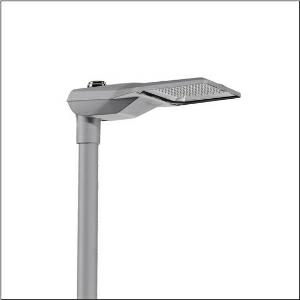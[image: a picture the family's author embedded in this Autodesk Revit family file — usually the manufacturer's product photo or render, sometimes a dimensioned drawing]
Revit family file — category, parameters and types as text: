
# Revit family: streetlight_sl_21_midi___p1_0a_5xe7a47n08mb_40bb
name_source: partatom
category: Lighting Fixtures
units: mm (PartAtom-declared; Revit-internal decimal feet)

## family parameters
Cut with Voids When Loaded = No
Host = Face
Light Source = No
Part Type = Normal
Room Calculation Point = No
Round Connector Dimension = Use Diameter
Shared = No

## types (1)
- --- (1 x LED, 20180 lm, 147 W, 4000K)
    Apparent Load = 147 VA
    CIE Flux Codes = 21 50 90 100 100
    Color Rendering = 70
    Color Temperature = 4000K
    Default Elevation = 1800 mm
    Description = Streetlight SL 21 midi, mast luminaire, primary light control with lens, of PMMA, primary optical cover: cover, of toughened safety glass, transparent, light distribution: P1.0a, light emission: direct distribution, primary light characteristic: asymmetric, installation type: side-entry, LED, 3G 2.5mm², High Power LED, rated luminous flux: 20.180lm, luminous efficacy: 137lm/W, light colour: 740, colour temperature: 4000K, control gear: NEMA (7pin), control: overheat protection, pre-setting: linear dimming characteristic, constant luminous flux control, time-dependent luminous flux control, flexible luminous flux parameterisation, mains connection: 220..240V, AC, 50/60Hz, connection cable pre-assembled, cable length: 12,5m, wiring characteristics: H05VV-F, start of lifetime: 147W, end of service life: 155W, reduction: 65W, luminaire housing, of diecast aluminium (EN AC-44300), powder-coated, Siteco® metallic grey (DB 702S), corrosivity category C5 mid according to DIN EN ISO 12944, multi-level sealing system, sealing non-destructively replaceable, inclination adjustable: 0°, 5°, 10°, 15°, length: 644mm, width: 335mm, height: 110mm, spigot size: 42mm (side-entry), mounting height: 4..8m, protection rating (complete): IP66, insulation class (complete): insulation class I (protective earthing), certification: CE, ENEC, ENEC+, VDE, impact resistance: IK10, permissible operating ambient temperature for outdoor applications: -40..+50°C, standard-compliant lighting for roads and squares, packaging unit: 1 piece

Light Distribution: P1.0a
    Height = 111 mm
    Lamp = 1 x LED
    Lamp Light Flux = 20180 lm
    Lamp Power = 147 W
    Lamp count = 1
    Length = 644 mm
    Luminous efficacy = 137 lm/W
    Manufacturer = Siteco
    ModVariant = No
    Model = 5XE7A47N08MB
    Number of Poles = 1
    OnlyDefault = Yes
    Power Factor = 1
    Product Name = Streetlight SL 21 midi | P1.0a
    Product group = mast luminaire | pylon top
    ProductGroupID = 6100
    Protection Class = Protection class I
    Protection Degree = IP 66
    RLX_Detail_Level = 1
    RLX_Emergency_Light_Flux = 0 lm
    RLX_Emergency_Type = 0
    RLX_Emergency_Type_DB = No
    RlxData = <blob elided: 37785 chars, md5=b732701b>
    Socket = socket
    Standby Power = 0 W
    System Light Flux = 20180 lm
    System Power = 147 W
    Type Comments = factory setting: luminous flux: 100 % | dim-lin: 254 | 750 mA
    Type Image = l_1294377.jpg
    URL = http://relux.com
    VarID = @adj_155923
    Voltage = 0 V
    Weight = 0.00 kg
    Width = 336 mm

## geometry (parser evidence)
native form markers: Blend x4, Sweep x12
no freeform markers — native parametric forms only
